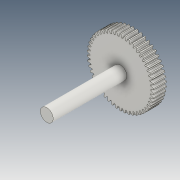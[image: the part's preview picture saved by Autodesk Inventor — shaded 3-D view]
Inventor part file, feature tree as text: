
AUTODESK INVENTOR PART (.ipt)
format: ipt  version: 2021 (Build 250183000, 183)  size: 334,848 bytes
history: native  units: mm (DEFAULTED — no unit token found)
features: plane x3, other x3, sketch x3, extrude x2
ambient origin geometry x8: Origin, YZ Plane, XZ Plane, XY Plane, X Axis, Y Axis, Z Axis, Center Point
bodies: Solid1 (feature_tree)
feature tree (11):
  extrude  "Extrusion1"  Depth=2.0mm TaperAngle=0.0deg
  plane  "Work Plane2"
  plane  "Work Plane8"
  plane  "Work Plane9"
  other  "Engrenagem reta"
  extrude  "Extrusão2"  Depth=10.0mm TaperAngle=0.0deg
  sketch  "Sketch1"  dims[d0=10.4mm d1=2.0mm d2=0.0mm]
  sketch  "Sketch2"  dims[d3=10.0mm d4=10.0mm d5=0.0mm]
  other  "Srf1"
  sketch  "Esboço3"  dims[d16=10.7mm d17=0.0mm d34=0.628319mm d39=0.0mm d41=0.0mm d43=10.7mm d46=10.7mm d47=0.0mm d48=0.0mm d49=11.5mm d50=0.0mm d51=0.5mm d52=0.872665mm]
  other  "Diâmetro do flanco"
